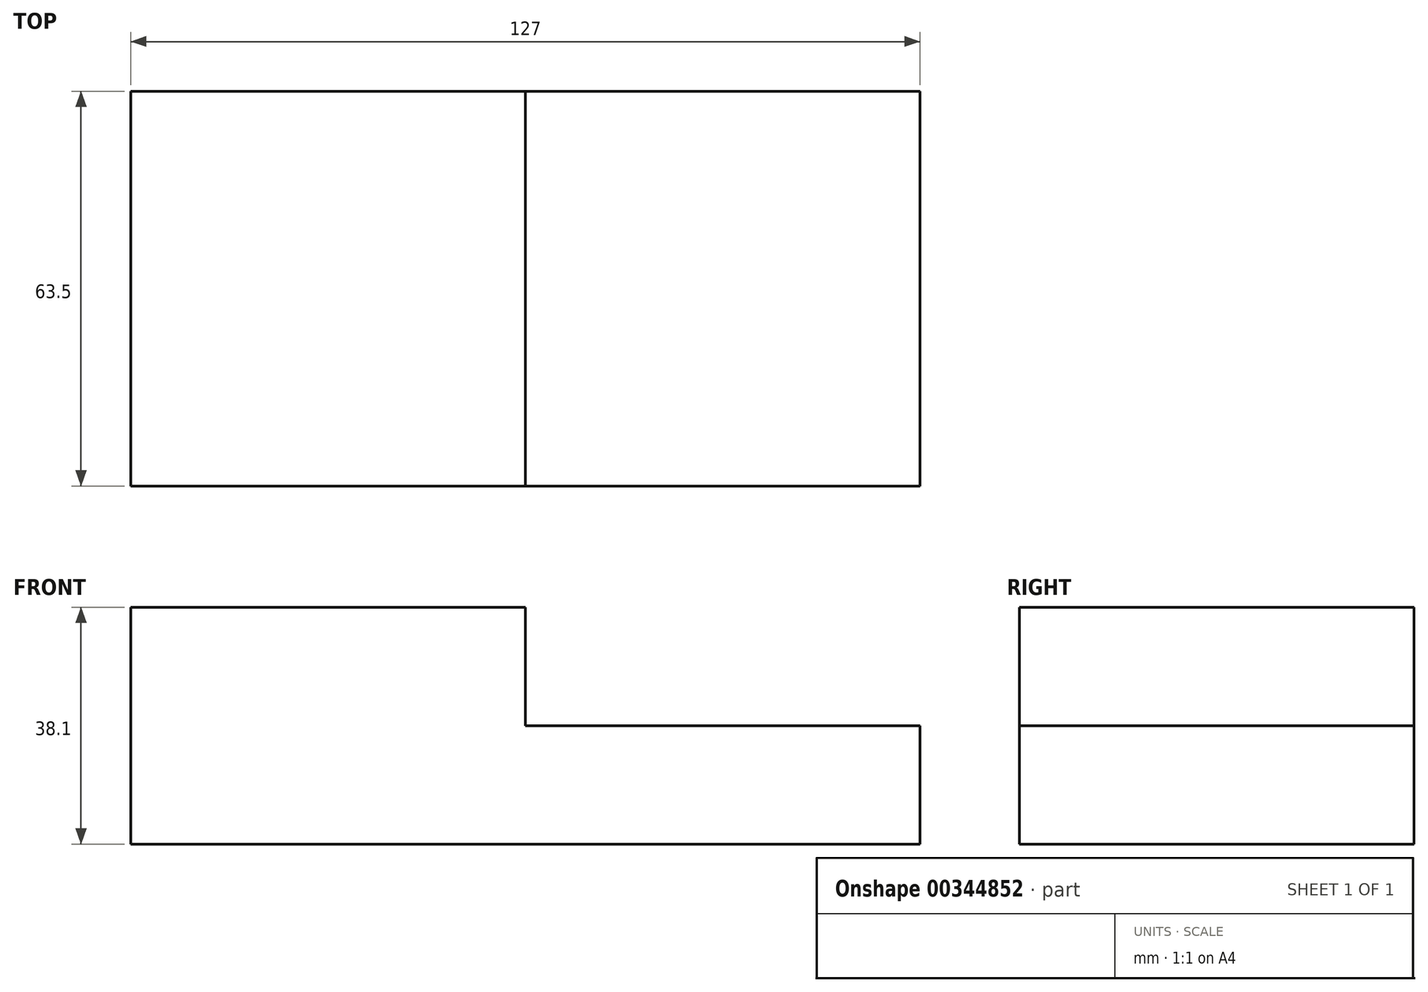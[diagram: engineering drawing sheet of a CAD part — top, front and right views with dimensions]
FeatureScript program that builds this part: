
annotation { "Feature Type Name" : "Feature", "Feature Type Description" : "" }
export const myFeature = defineFeature(function(context is Context, id is Id, definition is map)
    precondition{}
    {
        {
            var Q0;
            Q0=qCreatedBy(makeId("Front.planeOp"),FACE);
            var sketch = newSketch(context, id + "F0", { "sketchPlane" : qUnion([Q0])});
            skLineSegment(sketch, "E0.bottom", {"start": v(0, 0) * mm, "end": v(-127, 0) * mm});
            skLineSegment(sketch, "E0.top", {"start": v(0, -19.05) * mm, "end": v(-127, -19.05) * mm});
            skLineSegment(sketch, "E0.left", {"start": v(0, 0) * mm, "end": v(0, -19.05) * mm});
            skLineSegment(sketch, "E0.right", {"start": v(-127, 0) * mm, "end": v(-127, -19.05) * mm});
            skLineSegment(sketch, "E1.bottom", {"start": v(-127, 0) * mm, "end": v(-63.5, 0) * mm});
            skLineSegment(sketch, "E1.top", {"start": v(-127, 19.05) * mm, "end": v(-63.5, 19.05) * mm});
            skLineSegment(sketch, "E1.left", {"start": v(-127, 0) * mm, "end": v(-127, 19.05) * mm});
            skLineSegment(sketch, "E1.right", {"start": v(-63.5, 0) * mm, "end": v(-63.5, 19.05) * mm});
            skSolve(sketch);
        }
        {
            var Q0;
            Q0 = qSketchRegion(id + "F0", true);
            extrude(context, id + "F1", {"entities" : qUnion([Q0]), "depth" : 63.5 * mm});
        }
    });
